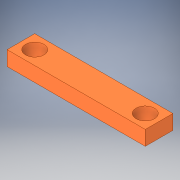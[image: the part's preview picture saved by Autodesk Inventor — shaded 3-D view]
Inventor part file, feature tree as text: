
AUTODESK INVENTOR PART (.ipt)
format: ipt  version: 2019 (Build 230136000, 136)  size: 117,248 bytes
history: native  units: mm
features: extrude x1, sketch x1
ambient origin geometry x8: Origin, YZ Plane, XZ Plane, XY Plane, X Axis, Y Axis, Z Axis, Center Point
bodies: Solid1 (feature_tree)
feature tree (2):
  extrude  "Extrusion1"  Depth=6.0mm
  sketch  "Sketch1"  dims[d0=30.0mm d1=6.0mm d2=4.0mm d3=4.0mm d4=3.0mm d5=3.0mm d6=3.0mm d7=3.0mm d8=3.18mm d9=0.0mm]
